# Revit family: R-MTD-309
name_source: partatom
category: Portes
units: mm (PartAtom-declared; Revit-internal decimal feet)

## family parameters
Couper avec des vides une fois chargée = Non
Hôte = Mur
Partagée = Non
Repère de localisation dans la pièce = Non
Toujours verticalement = Oui

## types (2) — shared parameters
Angle Rail 1 = 1.00°
Angle Rail 2 = 1.00°
Butée en U = Non
Construction analytique = <Aucun>
DC Fixation_Rail = 150 mm  [stored 0.492126 ft]
Ep Butée = 178 mm  [stored 0.58399 ft]
Ep Chicane Murale = 200 mm  [stored 0.656168 ft]
Ep Face Coté Baie = 10 mm  [stored 0.0328084 ft]
Ep Face Coté Opposé Baie = 10 mm  [stored 0.0328084 ft]
Ep Fond Butée = 11 mm  [stored 0.0360892 ft]
Ep Rail = 3 mm  [stored 0.00984252 ft]
Ep Vantail = 82 mm  [stored 0.269029 ft]
Fabricant = MALERBA
Grille Vantail Principal = Non
Grille Vantail Secondaire = Non
Grille toute hauteur = Non
Hauteur Baie = 2300 mm
Hauteur Profil Rail = 44 mm
Hauteur chandelle support grille = 180 mm  [stored 0.590551 ft]
Hauteur sous Dalle = 2500 mm  [stored 8.2021 ft]
Ht Fixation Linteau = 430 mm
Jeu Portillon Bas = 51 mm
Jeu Portillon Coté Opposé Pivot = 10 mm  [stored 0.0328084 ft]
Jeu Portillon Coté Pivot = 10 mm  [stored 0.0328084 ft]
Jeu Portillon Haut = 10 mm  [stored 0.0328084 ft]
Jeu Vantail Bas = 10 mm  [stored 0.0328084 ft]
Larg Portillon = 900 mm  [stored 2.95276 ft]
Larg Vantail Primaire Asymétrique = 2400 mm
Mat Ame = Prépeint
Mat Grille = Grille
Mat Quinc = Acier galvanisé
Mat Support = Peinture Laquée PMT - Gris Anthracite - RAL 7016
Materiaux_Dominant = Métal
Montage sur Mur Perpendiculaire = Non
Position Vantail Mur = 91 mm  [stored 0.298556 ft]
Prof Butée = 260 mm  [stored 0.853018 ft]
Prof Chicane Murale = 50 mm  [stored 0.164042 ft]
Prof Coté Butée = 71 mm
Profondeur Rail = 49 mm  [stored 0.160761 ft]
Rec Arrière = 215 mm
Rec Avant = 160 mm  [stored 0.524934 ft]
Rec Haut = 200 mm  [stored 0.656168 ft]
Retours Rails = 17 mm
URL = https://www.malerba.fr
Vantaux Asymétriques = Non
zero-valued in all types: DC Jeu Avant, DC Jeu Haut, DC Portillon, DC Profil Butée, Désax 2V Asymétrique, Thermique (W/m2.°K)

## per-type parameters (varying)
| type | 1 Vantail | 2 Vantaux | Butée en L | Certification | Code_MAJ | DAS | Description | Fiche_Produit | Fixation Linteau | Fixation sous Dalle | Ht Portillon | Largeur Baie | Lgt Fix Vantail Primaire | Lgt Fix Vantail Second | Lgt Rail Second | Modèle | Note d'identification | Reference_Commerciale | Resistance_Feu | Sens_Feu | lgt Rail Primaire |
| MTD-309 | Non | Oui | Non | D.A.S. Mode 2 certifié NF | 2411190104MTD309 | Oui | Bloc-porte métal industriel D.A.S. M 1202 S - DAS système coulissant à rencontre composés de 2 modules coulissants de 2 panneaux en hauteur, EI120, D.A.S. certifié NF, sur rail incliné ou droit, avec guidage au sol | MTD-309 | Oui | Non | 2300 mm | 4000 mm  [stored 13.1234 ft] | 4050 mm  [stored 13.2874 ft] | 4050 mm  [stored 13.2874 ft] | 4550 mm  [stored 14.9278 ft] | 18-Coulissante | 2V EI120 - DAS COULISSANT A RENCONTRE - 2 PANNEAUX | M1202S-DAS | EI120 | Recto / Verso | 4550 mm  [stored 14.9278 ft] |
| 17 - Coulissante 2 | Oui | Non | Oui |  |  | Non |  |  | Non | Oui | 2000 mm  [stored 6.56168 ft] | 5000 mm  [stored 16.4042 ft] | 10325 mm | 10325 mm | 10825 mm |  |  |  |  |  | 10825 mm |

note: [stored X ft] marks values corroborated as IEEE doubles in the binary element streams (Revit-internal decimal feet)

## geometry (parser evidence)
native form markers: Blend x12
no freeform markers — native parametric forms only
